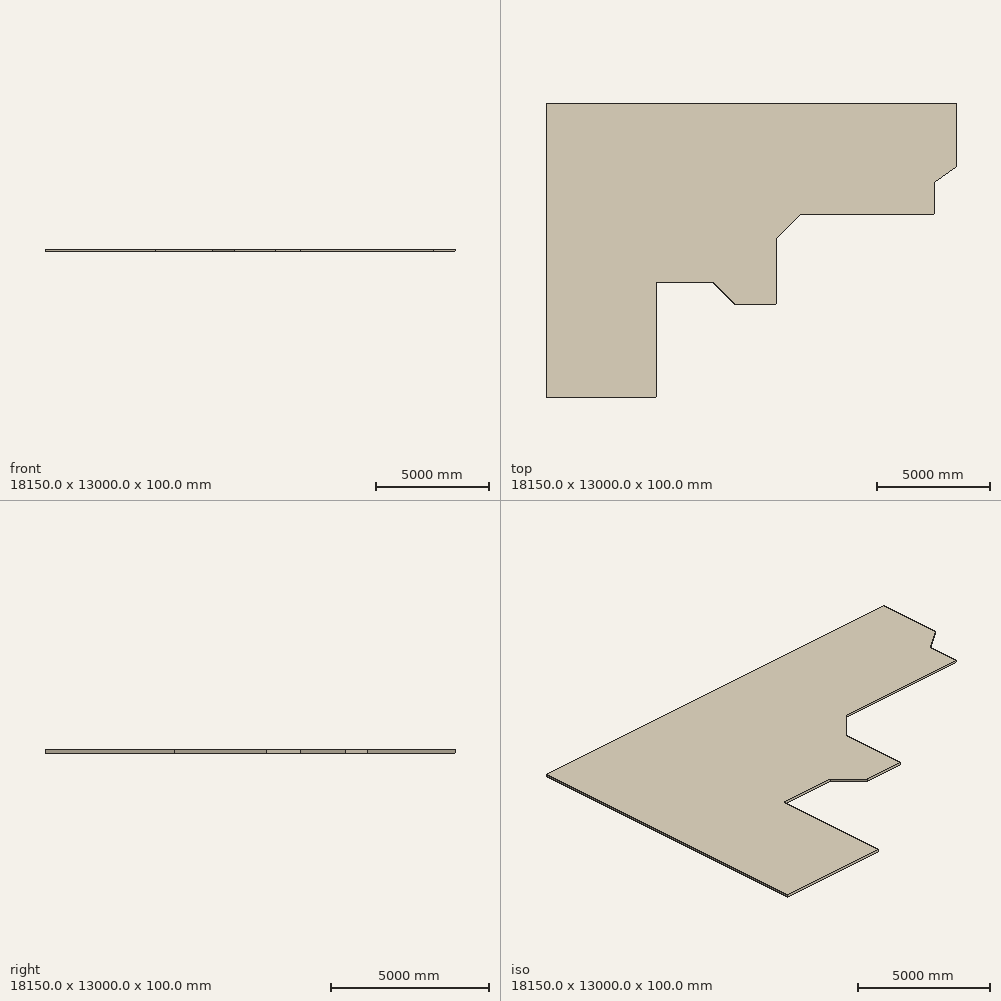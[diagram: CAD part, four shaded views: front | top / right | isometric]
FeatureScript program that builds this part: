
annotation { "Feature Type Name" : "Feature", "Feature Type Description" : "" }
export const myFeature = defineFeature(function(context is Context, id is Id, definition is map)
    precondition{}
    {
        {
            var Q0;
            Q0=qCreatedBy(makeId("Top.planeOp"),FACE);
            var sketch = newSketch(context, id + "F0", { "sketchPlane" : qUnion([Q0])});
            skLineSegment(sketch, "E0", {"start": v(7377.92, 9000) * mm, "end": v(6402.92, 9000) * mm});
            skLineSegment(sketch, "E1", {"start": v(6402.92, 9000) * mm, "end": v(5552.92, 9000) * mm});
            skLineSegment(sketch, "E2", {"start": v(702.92, 9000) * mm, "end": v(-597.08, 9000) * mm});
            skLineSegment(sketch, "E3", {"start": v(-597.08, 9000) * mm, "end": v(-2397.08, 9000) * mm});
            skLineSegment(sketch, "E4", {"start": v(-2397.08, 9000) * mm, "end": v(-5897.08, 9000) * mm});
            skLineSegment(sketch, "E5", {"start": v(-5897.08, 9000) * mm, "end": v(-10772.08, 9000) * mm});
            skLineSegment(sketch, "E6", {"start": v(-10772.08, -4000) * mm, "end": v(-5897.08, -4000) * mm});
            skLineSegment(sketch, "E7", {"start": v(-5897.08, -4000) * mm, "end": v(-5897.08, 1100) * mm});
            skLineSegment(sketch, "E8", {"start": v(-5897.08, 1100) * mm, "end": v(-3397.08, 1100) * mm});
            skLineSegment(sketch, "E9", {"start": v(-3397.08, 1100) * mm, "end": v(-2397.08, 100) * mm});
            skLineSegment(sketch, "E10", {"start": v(-2397.08, 100) * mm, "end": v(-597.08, 100) * mm});
            skLineSegment(sketch, "E11", {"start": v(-597.08, 100) * mm, "end": v(-597.08, 3000) * mm});
            skLineSegment(sketch, "E12", {"start": v(-597.08, 3000) * mm, "end": v(502.92, 4100) * mm});
            skLineSegment(sketch, "E13", {"start": v(502.92, 4100) * mm, "end": v(6402.92, 4100) * mm});
            skLineSegment(sketch, "E14", {"start": v(6402.92, 4100) * mm, "end": v(6402.92, 5500.45) * mm});
            skLineSegment(sketch, "E15", {"start": v(6402.92, 5500.45) * mm, "end": v(7377.92, 6200) * mm});
            skLineSegment(sketch, "E16", {"start": v(7377.92, 6200) * mm, "end": v(7377.92, 9000) * mm});
            skLineSegment(sketch, "E17", {"start": v(-10772.08, 9000) * mm, "end": v(-10772.08, 7800) * mm});
            skLineSegment(sketch, "E18", {"start": v(-10772.08, 7800) * mm, "end": v(-10772.08, 7000) * mm});
            skLineSegment(sketch, "E19", {"start": v(-10772.08, 7000) * mm, "end": v(-10772.08, 4100) * mm});
            skLineSegment(sketch, "E20", {"start": v(-10772.08, 4100) * mm, "end": v(-10772.08, 2800) * mm});
            skLineSegment(sketch, "E21", {"start": v(-10772.08, 2800) * mm, "end": v(-10772.08, 2100) * mm});
            skLineSegment(sketch, "E22", {"start": v(-10772.08, 2100) * mm, "end": v(-10772.08, 1100) * mm});
            skLineSegment(sketch, "E23", {"start": v(-10772.08, 1100) * mm, "end": v(-10772.08, 0) * mm});
            skLineSegment(sketch, "E24", {"start": v(-10772.08, 0) * mm, "end": v(-10772.08, -1000) * mm});
            skLineSegment(sketch, "E25", {"start": v(-10772.08, -1000) * mm, "end": v(-10772.08, -1200) * mm});
            skLineSegment(sketch, "E26", {"start": v(-10772.08, -1200) * mm, "end": v(-10772.08, -4000) * mm});
            skLineSegment(sketch, "E27", {"start": v(702.92, 9000) * mm, "end": v(3552.92, 9000) * mm});
            skLineSegment(sketch, "E28", {"start": v(3552.92, 9000) * mm, "end": v(5552.92, 9000) * mm});
            skSolve(sketch);
        }
        {
            var Q0;
            Q0 = qSketchRegion(id + "F0", true);
            extrude(context, id + "F1", {"entities" : qUnion([Q0]), "depth" : 100 * mm, "offsetDistance" : 25 * mm});
        }
    });
